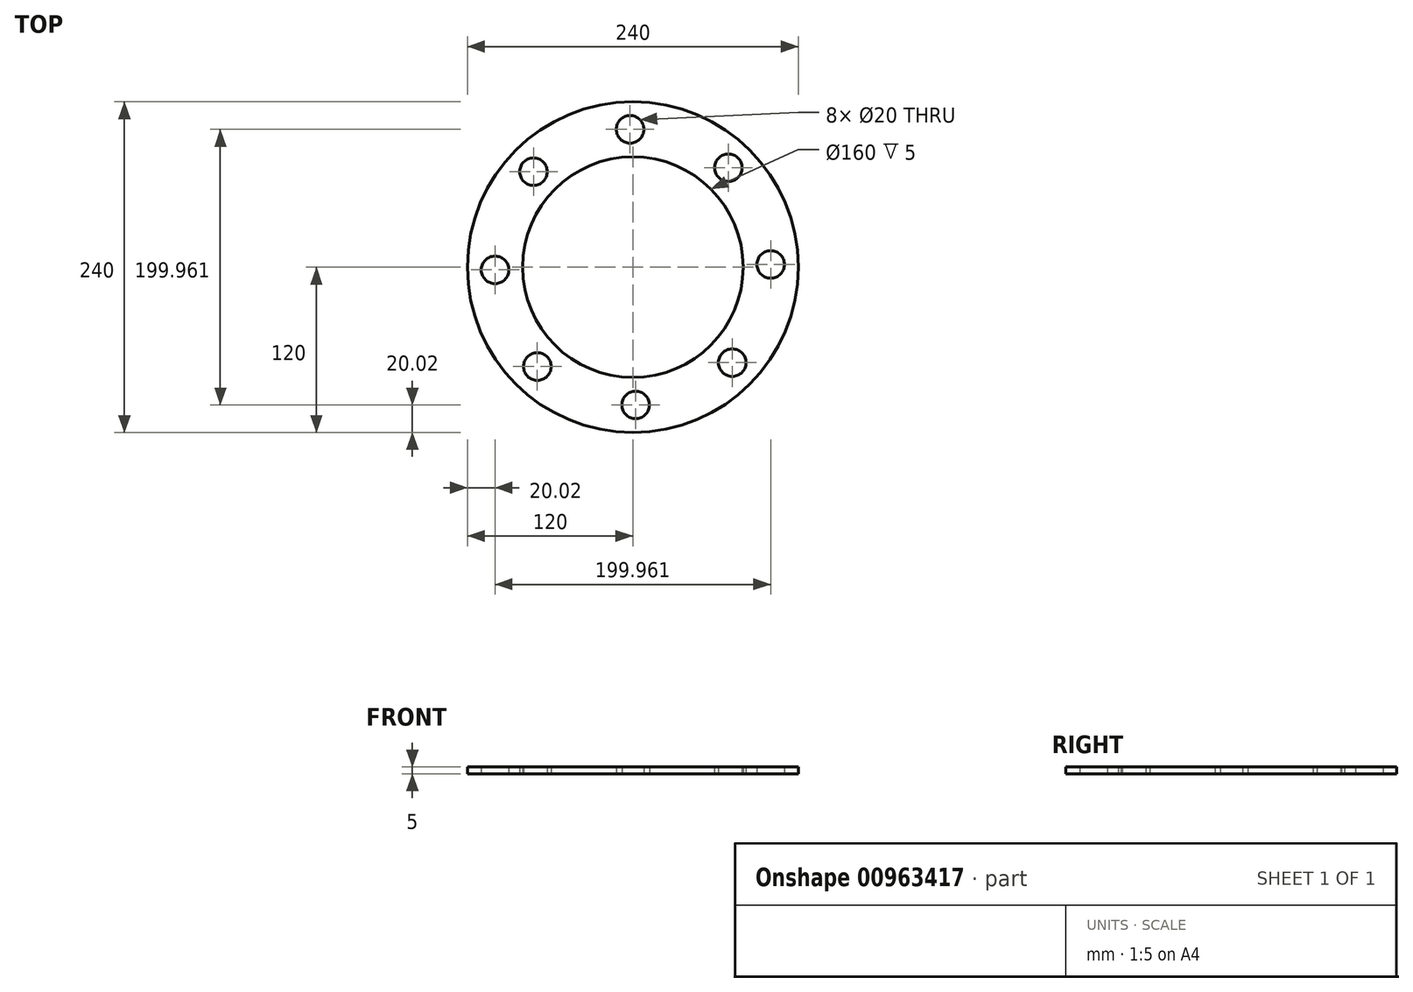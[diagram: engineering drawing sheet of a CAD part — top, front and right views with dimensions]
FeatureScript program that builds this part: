
annotation { "Feature Type Name" : "Feature", "Feature Type Description" : "" }
export const myFeature = defineFeature(function(context is Context, id is Id, definition is map)
    precondition{}
    {
        {
            var Q0;
            Q0=qCreatedBy(makeId("Top.planeOp"),FACE);
            var sketch = newSketch(context, id + "F0", { "sketchPlane" : qUnion([Q0])});
            skCircle(sketch, "E0", {"center": v(0, 0) * mm, "radius": 80 * mm});
            skCircle(sketch, "E1", {"center": v(0, 0) * mm, "radius": 100 * mm});
            skCircle(sketch, "E2", {"center": v(0, 0) * mm, "radius": 120 * mm});
            skCircle(sketch, "E3.cCircle", {"center": v(0, 0) * mm, "radius": 100 * mm, "construction": true});
            skCircle(sketch, "E4", {"center": v(-72.1, 69.3) * mm, "radius": 10 * mm});
            skCircle(sketch, "E5", {"center": v(-99.98, -1.99) * mm, "radius": 10 * mm});
            skCircle(sketch, "E6", {"center": v(-1.99, 99.98) * mm, "radius": 10 * mm});
            skCircle(sketch, "E7", {"center": v(69.3, 72.1) * mm, "radius": 10 * mm});
            skCircle(sketch, "E8", {"center": v(99.98, 1.99) * mm, "radius": 10 * mm});
            skCircle(sketch, "E9", {"center": v(72.1, -69.3) * mm, "radius": 10 * mm});
            skCircle(sketch, "E10", {"center": v(1.99, -99.98) * mm, "radius": 10 * mm});
            skCircle(sketch, "E11", {"center": v(-69.3, -72.1) * mm, "radius": 10 * mm});
            skSolve(sketch);
        }
        {
            var Q0;
            Q0=makeQuery(id+"F0.imprint","IMPRINT",FACE,{"disambiguationData":[TD([[makeQuery(id+"F0.imprint","IMPRINT",EDGE,{"derivedFrom":sQuery(id+"F0.wireOp",EDGE,"E2")}),1.0]])]});
            extrude(context, id + "F1", {"entities" : qUnion([Q0]), "depth" : 5 * mm, "offsetDistance" : 25 * mm});
        }
        {
            var Q0;
            Q0=makeQuery(id+"F0.imprint","IMPRINT",FACE,{"disambiguationData":[TD([[makeQuery(id+"F0.imprint","IMPRINT",EDGE,{"derivedFrom":sQuery(id+"F0.wireOp",EDGE,"E0")}),-1.0]])]});
            extrude(context, id + "F2", {"entities" : qUnion([Q0]), "operationType" : NewBodyOperationType.ADD, "depth" : 5 * mm, "offsetDistance" : 25 * mm});
        }
    });
